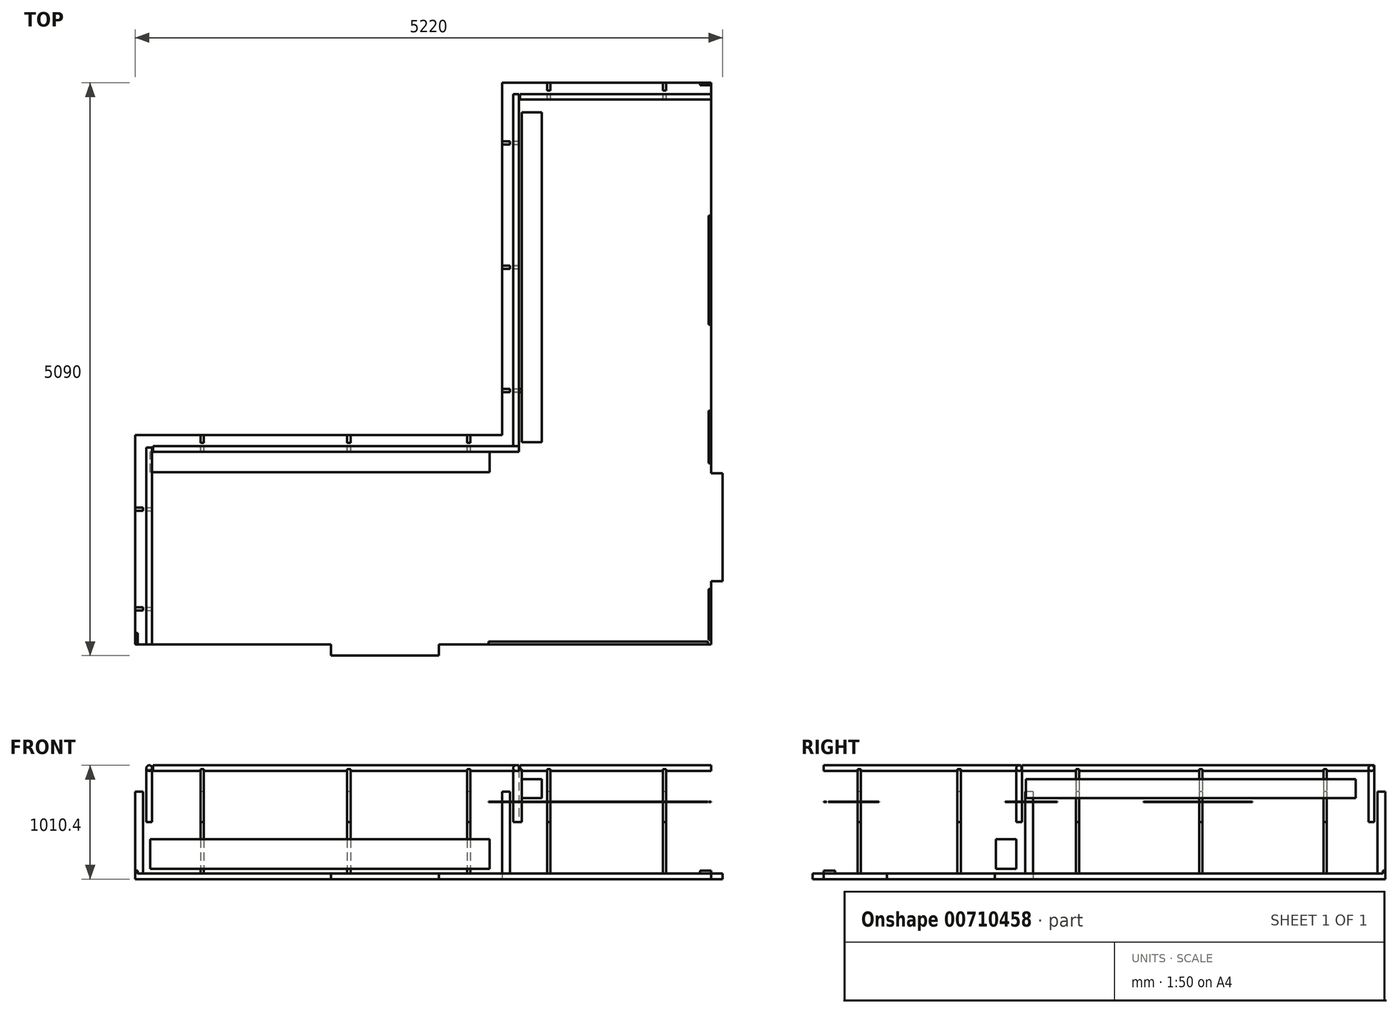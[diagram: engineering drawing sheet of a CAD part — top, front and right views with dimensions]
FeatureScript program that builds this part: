
annotation { "Feature Type Name" : "Feature", "Feature Type Description" : "" }
export const myFeature = defineFeature(function(context is Context, id is Id, definition is map)
    precondition{}
    {
        {
            var Q0;
            Q0=qCreatedBy(makeId("Top.planeOp"),FACE);
            var sketch = newSketch(context, id + "F0", { "sketchPlane" : qUnion([Q0])});
            skLineSegment(sketch, "E0", {"start": v(0, 0) * mm, "end": v(0, 560) * mm});
            skLineSegment(sketch, "E1", {"start": v(0, 4990) * mm, "end": v(-1860, 4990) * mm});
            skLineSegment(sketch, "E2", {"start": v(-1860, 4990) * mm, "end": v(-1860, 1860) * mm});
            skLineSegment(sketch, "E3", {"start": v(-1860, 1860) * mm, "end": v(-5120, 1860) * mm});
            skLineSegment(sketch, "E4", {"start": v(-5120, 1860) * mm, "end": v(-5120, 0) * mm});
            skLineSegment(sketch, "E5", {"start": v(-5120, 0) * mm, "end": v(-3380, 0) * mm});
            skLineSegment(sketch, "E6", {"start": v(0, 1520) * mm, "end": v(100, 1520) * mm});
            skLineSegment(sketch, "E7", {"start": v(100, 1520) * mm, "end": v(100, 560) * mm});
            skLineSegment(sketch, "E8", {"start": v(100, 560) * mm, "end": v(0, 560) * mm});
            skLineSegment(sketch, "E9.trimOffspring", {"start": v(0, 1520) * mm, "end": v(0, 4990) * mm});
            skLineSegment(sketch, "E10.trimOffspring", {"start": v(-2420, 0) * mm, "end": v(0, 0) * mm});
            skLineSegment(sketch, "E11", {"start": v(-3380, 0) * mm, "end": v(-3380, -100) * mm});
            skLineSegment(sketch, "E12", {"start": v(-3380, -100) * mm, "end": v(-2420, -100) * mm});
            skLineSegment(sketch, "E13", {"start": v(-2420, -100) * mm, "end": v(-2420, 0) * mm});
            skSolve(sketch);
        }
        {
            var Q0;
            Q0=makeQuery(id+"F0.imprint","IMPRINT",FACE,{"disambiguationData":[TD([[makeQuery(id+"F0.imprint","IMPRINT",EDGE,{"derivedFrom":sQuery(id+"F0.wireOp",EDGE,"E0")}),1.0]])]});
            extrude(context, id + "F1", {"entities" : qUnion([Q0]), "depth" : 25.4 * mm, "offsetDistance" : 25.4 * mm});
        }
        {
            var Q0;
            Q0=makeQuery(id+"F1.opExtrude","CAP_FACE",FACE,{"disambiguationData":[OSD([sQuery(id+"F0.wireOp",EDGE,"E0"),sQuery(id+"F0.wireOp",EDGE,"E1"),sQuery(id+"F0.wireOp",EDGE,"E2"),sQuery(id+"F0.wireOp",EDGE,"E3"),sQuery(id+"F0.wireOp",EDGE,"E4"),sQuery(id+"F0.wireOp",EDGE,"E5"),sQuery(id+"F0.wireOp",EDGE,"E6"),sQuery(id+"F0.wireOp",EDGE,"E7"),sQuery(id+"F0.wireOp",EDGE,"E8"),sQuery(id+"F0.wireOp",EDGE,"E9.trimOffspring"),sQuery(id+"F0.wireOp",EDGE,"E10.trimOffspring"),sQuery(id+"F0.wireOp",EDGE,"E11"),sQuery(id+"F0.wireOp",EDGE,"E12"),sQuery(id+"F0.wireOp",EDGE,"E13")])],"isStart":false});
            var sketch = newSketch(context, id + "F2", { "sketchPlane" : qUnion([Q0])});
            skLineSegment(sketch, "E14.bottom", {"start": v(-430, 4990) * mm, "end": v(-400, 4990) * mm});
            skLineSegment(sketch, "E14.top", {"start": v(-430, 4920) * mm, "end": v(-400, 4920) * mm});
            skLineSegment(sketch, "E14.left", {"start": v(-430, 4990) * mm, "end": v(-430, 4920) * mm});
            skLineSegment(sketch, "E14.right", {"start": v(-400, 4990) * mm, "end": v(-400, 4920) * mm});
            skLineSegment(sketch, "E15.bottom", {"start": v(-1860, 4470) * mm, "end": v(-1790, 4470) * mm});
            skLineSegment(sketch, "E15.top", {"start": v(-1860, 4440) * mm, "end": v(-1790, 4440) * mm});
            skLineSegment(sketch, "E15.left", {"start": v(-1860, 4470) * mm, "end": v(-1860, 4440) * mm});
            skLineSegment(sketch, "E15.right", {"start": v(-1790, 4470) * mm, "end": v(-1790, 4440) * mm});
            skLineSegment(sketch, "E16.bottom", {"start": v(-1860, 2270) * mm, "end": v(-1790, 2270) * mm});
            skLineSegment(sketch, "E16.top", {"start": v(-1860, 2240) * mm, "end": v(-1790, 2240) * mm});
            skLineSegment(sketch, "E16.left", {"start": v(-1860, 2270) * mm, "end": v(-1860, 2240) * mm});
            skLineSegment(sketch, "E16.right", {"start": v(-1790, 2270) * mm, "end": v(-1790, 2240) * mm});
            skLineSegment(sketch, "E17.bottom", {"start": v(-2171.25, 1860) * mm, "end": v(-2141.25, 1860) * mm});
            skLineSegment(sketch, "E17.top", {"start": v(-2171.25, 1790) * mm, "end": v(-2141.25, 1790) * mm});
            skLineSegment(sketch, "E17.left", {"start": v(-2171.25, 1860) * mm, "end": v(-2171.25, 1790) * mm});
            skLineSegment(sketch, "E17.right", {"start": v(-2141.25, 1860) * mm, "end": v(-2141.25, 1790) * mm});
            skLineSegment(sketch, "E18.bottom", {"start": v(-3235.69, 1860) * mm, "end": v(-3205.69, 1860) * mm});
            skLineSegment(sketch, "E18.top", {"start": v(-3235.69, 1790) * mm, "end": v(-3205.69, 1790) * mm});
            skLineSegment(sketch, "E18.left", {"start": v(-3235.69, 1860) * mm, "end": v(-3235.69, 1790) * mm});
            skLineSegment(sketch, "E18.right", {"start": v(-3205.69, 1860) * mm, "end": v(-3205.69, 1790) * mm});
            skLineSegment(sketch, "E19.bottom", {"start": v(-4538.86, 1860) * mm, "end": v(-4508.86, 1860) * mm});
            skLineSegment(sketch, "E19.top", {"start": v(-4538.86, 1790) * mm, "end": v(-4508.86, 1790) * mm});
            skLineSegment(sketch, "E19.left", {"start": v(-4538.86, 1860) * mm, "end": v(-4538.86, 1790) * mm});
            skLineSegment(sketch, "E19.right", {"start": v(-4508.86, 1860) * mm, "end": v(-4508.86, 1790) * mm});
            skLineSegment(sketch, "E20.bottom", {"start": v(-1460, 4990) * mm, "end": v(-1430, 4990) * mm});
            skLineSegment(sketch, "E20.top", {"start": v(-1460, 4920) * mm, "end": v(-1430, 4920) * mm});
            skLineSegment(sketch, "E20.left", {"start": v(-1460, 4990) * mm, "end": v(-1460, 4920) * mm});
            skLineSegment(sketch, "E20.right", {"start": v(-1430, 4990) * mm, "end": v(-1430, 4920) * mm});
            skLineSegment(sketch, "E21.bottom", {"start": v(-5120, 300) * mm, "end": v(-5050, 300) * mm});
            skLineSegment(sketch, "E21.top", {"start": v(-5120, 330) * mm, "end": v(-5050, 330) * mm});
            skLineSegment(sketch, "E21.left", {"start": v(-5120, 300) * mm, "end": v(-5120, 330) * mm});
            skLineSegment(sketch, "E21.right", {"start": v(-5050, 300) * mm, "end": v(-5050, 330) * mm});
            skLineSegment(sketch, "E22.bottom", {"start": v(-1860, 3335) * mm, "end": v(-1790, 3335) * mm});
            skLineSegment(sketch, "E22.top", {"start": v(-1860, 3365) * mm, "end": v(-1790, 3365) * mm});
            skLineSegment(sketch, "E22.left", {"start": v(-1860, 3335) * mm, "end": v(-1860, 3365) * mm});
            skLineSegment(sketch, "E22.right", {"start": v(-1790, 3335) * mm, "end": v(-1790, 3365) * mm});
            skLineSegment(sketch, "E23.bottom", {"start": v(-5120, 1216.35) * mm, "end": v(-5050, 1216.35) * mm});
            skLineSegment(sketch, "E23.top", {"start": v(-5120, 1186.35) * mm, "end": v(-5050, 1186.35) * mm});
            skLineSegment(sketch, "E23.left", {"start": v(-5120, 1216.35) * mm, "end": v(-5120, 1186.35) * mm});
            skLineSegment(sketch, "E23.right", {"start": v(-5050, 1216.35) * mm, "end": v(-5050, 1186.35) * mm});
            skSolve(sketch);
        }
        {
            var Q0;
            Q0 = qSketchRegion(id + "F2", true);
            extrude(context, id + "F3", {"entities" : qUnion([Q0]), "operationType" : NewBodyOperationType.ADD, "depth" : 750 * mm, "offsetDistance" : 25 * mm});
        }
        {
            var Q0;
            Q0=makeQuery(id+"F1.opExtrude","CAP_FACE",FACE,{"disambiguationData":[OSD([sQuery(id+"F0.wireOp",EDGE,"E0"),sQuery(id+"F0.wireOp",EDGE,"E1"),sQuery(id+"F0.wireOp",EDGE,"E2"),sQuery(id+"F0.wireOp",EDGE,"E3"),sQuery(id+"F0.wireOp",EDGE,"E4"),sQuery(id+"F0.wireOp",EDGE,"E5"),sQuery(id+"F0.wireOp",EDGE,"E6"),sQuery(id+"F0.wireOp",EDGE,"E7"),sQuery(id+"F0.wireOp",EDGE,"E8"),sQuery(id+"F0.wireOp",EDGE,"E9.trimOffspring"),sQuery(id+"F0.wireOp",EDGE,"E10.trimOffspring"),sQuery(id+"F0.wireOp",EDGE,"E11"),sQuery(id+"F0.wireOp",EDGE,"E12"),sQuery(id+"F0.wireOp",EDGE,"E13")])],"isStart":false});
            cPlane(context, id + "F4", {"entities" : qUnion([Q0]), "cplaneType" : CPlaneType.OFFSET, "offset" : 480 * mm, "width" : 150 * mm, "height" : 150 * mm});
        }
        {
            var Q0;
            Q0=qCreatedBy(id+"F4.planeOp",FACE);
            var sketch = newSketch(context, id + "F5", { "sketchPlane" : qUnion([Q0])});
            skPoint(sketch, "E24.oppositeSnap0", {"position": v(-1825, 4470) * mm});
            skLineSegment(sketch, "E24.bottom", {"start": v(-1760, 4440) * mm, "end": v(-1710, 4440) * mm});
            skLineSegment(sketch, "E24.top", {"start": v(-1760, 4470) * mm, "end": v(-1710, 4470) * mm});
            skLineSegment(sketch, "E24.left", {"start": v(-1760, 4440) * mm, "end": v(-1760, 4470) * mm});
            skLineSegment(sketch, "E24.right", {"start": v(-1710, 4440) * mm, "end": v(-1710, 4470) * mm});
            skLineSegment(sketch, "E25.bottom", {"start": v(-1460, 4890) * mm, "end": v(-1430, 4890) * mm});
            skLineSegment(sketch, "E25.top", {"start": v(-1460, 4840) * mm, "end": v(-1430, 4840) * mm});
            skLineSegment(sketch, "E25.left", {"start": v(-1460, 4890) * mm, "end": v(-1460, 4840) * mm});
            skLineSegment(sketch, "E25.right", {"start": v(-1430, 4890) * mm, "end": v(-1430, 4840) * mm});
            skPoint(sketch, "E26.oppositeSnap0", {"position": v(-400, 4955) * mm});
            skLineSegment(sketch, "E26.bottom", {"start": v(-430, 4890) * mm, "end": v(-400, 4890) * mm});
            skLineSegment(sketch, "E26.top", {"start": v(-430, 4840) * mm, "end": v(-400, 4840) * mm});
            skLineSegment(sketch, "E26.left", {"start": v(-430, 4890) * mm, "end": v(-430, 4840) * mm});
            skLineSegment(sketch, "E26.right", {"start": v(-400, 4890) * mm, "end": v(-400, 4840) * mm});
            skLineSegment(sketch, "E27.bottom", {"start": v(-1760, 2270) * mm, "end": v(-1710, 2270) * mm});
            skLineSegment(sketch, "E27.top", {"start": v(-1760, 2240) * mm, "end": v(-1710, 2240) * mm});
            skLineSegment(sketch, "E27.left", {"start": v(-1760, 2270) * mm, "end": v(-1760, 2240) * mm});
            skLineSegment(sketch, "E27.right", {"start": v(-1710, 2270) * mm, "end": v(-1710, 2240) * mm});
            skLineSegment(sketch, "E28.bottom", {"start": v(-2171.25, 1760) * mm, "end": v(-2141.25, 1760) * mm});
            skLineSegment(sketch, "E28.top", {"start": v(-2171.25, 1710) * mm, "end": v(-2141.25, 1710) * mm});
            skLineSegment(sketch, "E28.left", {"start": v(-2171.25, 1760) * mm, "end": v(-2171.25, 1710) * mm});
            skLineSegment(sketch, "E28.right", {"start": v(-2141.25, 1760) * mm, "end": v(-2141.25, 1710) * mm});
            skLineSegment(sketch, "E29.bottom", {"start": v(-3235.69, 1710) * mm, "end": v(-3205.69, 1710) * mm});
            skLineSegment(sketch, "E29.top", {"start": v(-3235.69, 1760) * mm, "end": v(-3205.69, 1760) * mm});
            skLineSegment(sketch, "E29.left", {"start": v(-3235.69, 1710) * mm, "end": v(-3235.69, 1760) * mm});
            skLineSegment(sketch, "E29.right", {"start": v(-3205.69, 1710) * mm, "end": v(-3205.69, 1760) * mm});
            skLineSegment(sketch, "E30.bottom", {"start": v(-4538.86, 1760) * mm, "end": v(-4508.86, 1760) * mm});
            skLineSegment(sketch, "E30.top", {"start": v(-4538.86, 1710) * mm, "end": v(-4508.86, 1710) * mm});
            skLineSegment(sketch, "E30.left", {"start": v(-4538.86, 1760) * mm, "end": v(-4538.86, 1710) * mm});
            skLineSegment(sketch, "E30.right", {"start": v(-4508.86, 1760) * mm, "end": v(-4508.86, 1710) * mm});
            skLineSegment(sketch, "E31.bottom", {"start": v(-5020, 330) * mm, "end": v(-4970, 330) * mm});
            skLineSegment(sketch, "E31.top", {"start": v(-5020, 300) * mm, "end": v(-4970, 300) * mm});
            skLineSegment(sketch, "E31.left", {"start": v(-4970, 330) * mm, "end": v(-4970, 300) * mm});
            skLineSegment(sketch, "E31.right", {"start": v(-5020, 330) * mm, "end": v(-5020, 300) * mm});
            skLineSegment(sketch, "E32.bottom", {"start": v(-5020, 1216.35) * mm, "end": v(-4970, 1216.35) * mm});
            skLineSegment(sketch, "E32.top", {"start": v(-5020, 1186.35) * mm, "end": v(-4970, 1186.35) * mm});
            skLineSegment(sketch, "E32.left", {"start": v(-5020, 1216.35) * mm, "end": v(-5020, 1186.35) * mm});
            skLineSegment(sketch, "E32.right", {"start": v(-4970, 1216.35) * mm, "end": v(-4970, 1186.35) * mm});
            skLineSegment(sketch, "E33.bottom", {"start": v(-1760, 3365) * mm, "end": v(-1710, 3365) * mm});
            skLineSegment(sketch, "E33.top", {"start": v(-1760, 3335) * mm, "end": v(-1710, 3335) * mm});
            skLineSegment(sketch, "E33.left", {"start": v(-1760, 3365) * mm, "end": v(-1760, 3335) * mm});
            skLineSegment(sketch, "E33.right", {"start": v(-1710, 3365) * mm, "end": v(-1710, 3335) * mm});
            skSolve(sketch);
        }
        {
            var Q0;
            Q0 = qSketchRegion(id + "F5", true);
            extrude(context, id + "F6", {"entities" : qUnion([Q0]), "operationType" : NewBodyOperationType.ADD, "depth" : 470 * mm, "offsetDistance" : 25 * mm});
        }
        {
            var Q0;
            Q0=makeQuery(id+"F1.opExtrude","SWEPT_FACE",FACE,{"disambiguationData":[OSD([sQuery(id+"F0.wireOp",EDGE,"E9.trimOffspring")])]});
            var sketch = newSketch(context, id + "F7", { "sketchPlane" : qUnion([Q0])});
            skCircle(sketch, "E34", {"center": v(4865, 985.4) * mm, "radius": 25 * mm});
            skLineSegment(sketch, "E35", {"start": v(4865, 985.4) * mm, "end": v(4865, 975.4) * mm, "construction": true});
            skSolve(sketch);
        }
        {
            var Q0;
            Q0 = qSketchRegion(id + "F7", true);
            var Q1;
            Q1=makeQuery(id+"F3.boolean.opBoolean","MERGE",FACE,{"derivedFrom":[makeQuery(id+"F1.opExtrude","SWEPT_FACE",FACE,{"disambiguationData":[OSD([sQuery(id+"F0.wireOp",EDGE,"E2")])]}),makeQuery(id+"F3.opExtrude","SWEPT_FACE",FACE,{"disambiguationData":[OSD([sQuery(id+"F2.wireOp",EDGE,"E15.left")])]}),makeQuery(id+"F3.opExtrude","SWEPT_FACE",FACE,{"disambiguationData":[OSD([sQuery(id+"F2.wireOp",EDGE,"E16.left")])]})]});
            extrude(context, id + "F8", {"entities" : qUnion([Q0]), "operationType" : NewBodyOperationType.ADD, "oppositeDirection" : true, "depth" : 1700 * mm, "endBoundEntityFace" : qUnion([Q1]), "offsetDistance" : 25 * mm});
        }
        {
            var Q0;
            Q0=makeQuery(id+"F6.opExtrude","SWEPT_FACE",FACE,{"disambiguationData":[OSD([sQuery(id+"F5.wireOp",EDGE,"E25.bottom")])]});
            var sketch = newSketch(context, id + "F9", { "sketchPlane" : qUnion([Q0])});
            skCircle(sketch, "E36", {"center": v(1735, 985.4) * mm, "radius": 25 * mm});
            skLineSegment(sketch, "E37", {"start": v(1735, 985.4) * mm, "end": v(1735, 975.4) * mm, "construction": true});
            skSolve(sketch);
        }
        {
            var Q0;
            Q0=makeQuery(id+"F9.imprint","IMPRINT",FACE,{"disambiguationData":[TD([[makeQuery(id+"F9.imprint","IMPRINT",EDGE,{"derivedFrom":sQuery(id+"F9.wireOp",EDGE,"E36")}),1.0]])]});
            extrude(context, id + "F10", {"entities" : qUnion([Q0]), "operationType" : NewBodyOperationType.ADD, "oppositeDirection" : true, "depth" : 3130 * mm, "offsetDistance" : 25 * mm});
        }
        {
            var Q0;
            Q0=makeQuery(id+"F6.opExtrude","SWEPT_FACE",FACE,{"disambiguationData":[OSD([sQuery(id+"F5.wireOp",EDGE,"E27.right")])]});
            var sketch = newSketch(context, id + "F11", { "sketchPlane" : qUnion([Q0])});
            skCircle(sketch, "E38", {"center": v(1735, 985.4) * mm, "radius": 25 * mm});
            skLineSegment(sketch, "E39", {"start": v(1735, 985.4) * mm, "end": v(1735, 975.4) * mm, "construction": true});
            skSolve(sketch);
        }
        {
            var Q0;
            Q0 = qSketchRegion(id + "F11", true);
            var Q1;
            Q1=makeQuery(id+"F3.boolean.opBoolean","MERGE",FACE,{"derivedFrom":[makeQuery(id+"F1.opExtrude","SWEPT_FACE",FACE,{"disambiguationData":[OSD([sQuery(id+"F0.wireOp",EDGE,"E4")])]}),makeQuery(id+"F3.opExtrude","SWEPT_FACE",FACE,{"disambiguationData":[OSD([sQuery(id+"F2.wireOp",EDGE,"E21.left")])]}),makeQuery(id+"F3.opExtrude","SWEPT_FACE",FACE,{"disambiguationData":[OSD([sQuery(id+"F2.wireOp",EDGE,"E23.left")])]})]});
            extrude(context, id + "F12", {"entities" : qUnion([Q0]), "operationType" : NewBodyOperationType.ADD, "oppositeDirection" : true, "depth" : 3250 * mm, "endBoundEntityFace" : qUnion([Q1]), "offsetDistance" : 25 * mm});
        }
        {
            var Q0;
            Q0=makeQuery(id+"F1.opExtrude","SWEPT_FACE",FACE,{"disambiguationData":[OSD([sQuery(id+"F0.wireOp",EDGE,"E5")])]});
            var sketch = newSketch(context, id + "F13", { "sketchPlane" : qUnion([Q0])});
            skCircle(sketch, "E40", {"center": v(-4995, 985.4) * mm, "radius": 25 * mm});
            skLineSegment(sketch, "E41", {"start": v(-4995, 985.4) * mm, "end": v(-4995, 975.4) * mm, "construction": true});
            skSolve(sketch);
        }
        {
            var Q0;
            Q0 = qSketchRegion(id + "F13", true);
            var Q1;
            Q1=makeQuery(id+"F3.boolean.opBoolean","MERGE",FACE,{"derivedFrom":[makeQuery(id+"F1.opExtrude","SWEPT_FACE",FACE,{"disambiguationData":[OSD([sQuery(id+"F0.wireOp",EDGE,"E3")])]}),makeQuery(id+"F3.opExtrude","SWEPT_FACE",FACE,{"disambiguationData":[OSD([sQuery(id+"F2.wireOp",EDGE,"E17.bottom")])]}),makeQuery(id+"F3.opExtrude","SWEPT_FACE",FACE,{"disambiguationData":[OSD([sQuery(id+"F2.wireOp",EDGE,"E18.bottom")])]}),makeQuery(id+"F3.opExtrude","SWEPT_FACE",FACE,{"disambiguationData":[OSD([sQuery(id+"F2.wireOp",EDGE,"E19.bottom")])]})]});
            extrude(context, id + "F14", {"entities" : qUnion([Q0]), "oppositeDirection" : true, "depth" : 1750 * mm, "endBoundEntityFace" : qUnion([Q1]), "offsetDistance" : 25 * mm});
        }
        {
            var Q0;
            Q0=makeQuery(id+"F1.opExtrude","CAP_FACE",FACE,{"disambiguationData":[OSD([sQuery(id+"F0.wireOp",EDGE,"E0"),sQuery(id+"F0.wireOp",EDGE,"E1"),sQuery(id+"F0.wireOp",EDGE,"E2"),sQuery(id+"F0.wireOp",EDGE,"E3"),sQuery(id+"F0.wireOp",EDGE,"E4"),sQuery(id+"F0.wireOp",EDGE,"E5"),sQuery(id+"F0.wireOp",EDGE,"E6"),sQuery(id+"F0.wireOp",EDGE,"E7"),sQuery(id+"F0.wireOp",EDGE,"E8"),sQuery(id+"F0.wireOp",EDGE,"E9.trimOffspring"),sQuery(id+"F0.wireOp",EDGE,"E10.trimOffspring"),sQuery(id+"F0.wireOp",EDGE,"E11"),sQuery(id+"F0.wireOp",EDGE,"E12"),sQuery(id+"F0.wireOp",EDGE,"E13")])],"isStart":false});
            cPlane(context, id + "F15", {"entities" : qUnion([Q0]), "cplaneType" : CPlaneType.OFFSET, "offset" : 660 * mm, "width" : 150 * mm, "height" : 150 * mm});
        }
        {
            var Q0;
            Q0=qCreatedBy(id+"F15.planeOp",FACE);
            var sketch = newSketch(context, id + "F16", { "sketchPlane" : qUnion([Q0])});
            skLineSegment(sketch, "E42.bottom", {"start": v(0, 3810) * mm, "end": v(-25, 3810) * mm});
            skLineSegment(sketch, "E42.top", {"start": v(0, 2840) * mm, "end": v(-25, 2840) * mm});
            skLineSegment(sketch, "E42.left", {"start": v(0, 3810) * mm, "end": v(0, 2840) * mm});
            skLineSegment(sketch, "E42.right", {"start": v(-25, 3810) * mm, "end": v(-25, 2840) * mm});
            skLineSegment(sketch, "E43.bottom", {"start": v(0, 2075) * mm, "end": v(-25, 2075) * mm});
            skLineSegment(sketch, "E43.top", {"start": v(0, 1610) * mm, "end": v(-25, 1610) * mm});
            skLineSegment(sketch, "E43.left", {"start": v(0, 2075) * mm, "end": v(0, 1610) * mm});
            skLineSegment(sketch, "E43.right", {"start": v(-25, 2075) * mm, "end": v(-25, 1610) * mm});
            skLineSegment(sketch, "E44.bottom", {"start": v(-30, 0) * mm, "end": v(-1980, 0) * mm});
            skLineSegment(sketch, "E44.top", {"start": v(-30, 25) * mm, "end": v(-1980, 25) * mm});
            skLineSegment(sketch, "E44.left", {"start": v(-30, 0) * mm, "end": v(-30, 25) * mm});
            skLineSegment(sketch, "E44.right", {"start": v(-1980, 0) * mm, "end": v(-1980, 25) * mm});
            skLineSegment(sketch, "E45.bottom", {"start": v(0, 490) * mm, "end": v(-25, 490) * mm});
            skLineSegment(sketch, "E45.top", {"start": v(0, 40) * mm, "end": v(-25, 40) * mm});
            skLineSegment(sketch, "E45.left", {"start": v(0, 490) * mm, "end": v(0, 40) * mm});
            skLineSegment(sketch, "E45.right", {"start": v(-25, 490) * mm, "end": v(-25, 40) * mm});
            skSolve(sketch);
        }
        {
            var Q0;
            Q0 = qSketchRegion(id + "F16", true);
            extrude(context, id + "F17", {"entities" : qUnion([Q0]), "operationType" : NewBodyOperationType.ADD, "depth" : 3 * mm, "offsetDistance" : 25 * mm});
        }
        {
            var Q0;
            Q0=makeQuery(id+"F2.imprint","IMPRINT",FACE,{"disambiguationData":[TD([[makeQuery(id+"F2.imprint","IMPRINT",EDGE,{"derivedFrom":sQuery(id+"F2.wireOp",EDGE,"E14.top")}),-1.0]])]});
            extrude(context, id + "F18", {"entities" : qUnion([Q0]), "operationType" : NewBodyOperationType.ADD, "depth" : 25 * mm, "offsetDistance" : 25 * mm});
        }
        {
            var Q0;
            Q0=makeQuery(id+"F18.opExtrude","CAP_FACE",FACE,{"disambiguationData":[OSD([sQuery(id+"F0.wireOp",EDGE,"E0"),sQuery(id+"F0.wireOp",EDGE,"E1"),sQuery(id+"F0.wireOp",EDGE,"E2"),sQuery(id+"F0.wireOp",EDGE,"E3"),sQuery(id+"F0.wireOp",EDGE,"E4"),sQuery(id+"F0.wireOp",EDGE,"E5"),sQuery(id+"F0.wireOp",EDGE,"E6"),sQuery(id+"F0.wireOp",EDGE,"E7"),sQuery(id+"F0.wireOp",EDGE,"E8"),sQuery(id+"F0.wireOp",EDGE,"E9.trimOffspring"),sQuery(id+"F0.wireOp",EDGE,"E10.trimOffspring"),sQuery(id+"F0.wireOp",EDGE,"E11"),sQuery(id+"F0.wireOp",EDGE,"E12"),sQuery(id+"F0.wireOp",EDGE,"E13"),sQuery(id+"F2.wireOp",EDGE,"E14.top"),sQuery(id+"F2.wireOp",EDGE,"E14.left"),sQuery(id+"F2.wireOp",EDGE,"E14.right"),sQuery(id+"F2.wireOp",EDGE,"E15.bottom"),sQuery(id+"F2.wireOp",EDGE,"E15.top"),sQuery(id+"F2.wireOp",EDGE,"E15.right"),sQuery(id+"F2.wireOp",EDGE,"E16.bottom"),sQuery(id+"F2.wireOp",EDGE,"E16.top"),sQuery(id+"F2.wireOp",EDGE,"E16.right"),sQuery(id+"F2.wireOp",EDGE,"E17.top"),sQuery(id+"F2.wireOp",EDGE,"E17.left"),sQuery(id+"F2.wireOp",EDGE,"E17.right"),sQuery(id+"F2.wireOp",EDGE,"E18.top"),sQuery(id+"F2.wireOp",EDGE,"E18.left"),sQuery(id+"F2.wireOp",EDGE,"E18.right"),sQuery(id+"F2.wireOp",EDGE,"E19.top"),sQuery(id+"F2.wireOp",EDGE,"E19.left"),sQuery(id+"F2.wireOp",EDGE,"E19.right"),sQuery(id+"F2.wireOp",EDGE,"E20.top"),sQuery(id+"F2.wireOp",EDGE,"E20.left"),sQuery(id+"F2.wireOp",EDGE,"E20.right"),sQuery(id+"F2.wireOp",EDGE,"E21.bottom"),sQuery(id+"F2.wireOp",EDGE,"E21.top"),sQuery(id+"F2.wireOp",EDGE,"E21.right"),sQuery(id+"F2.wireOp",EDGE,"E22.bottom"),sQuery(id+"F2.wireOp",EDGE,"E22.top"),sQuery(id+"F2.wireOp",EDGE,"E22.right"),sQuery(id+"F2.wireOp",EDGE,"E23.bottom"),sQuery(id+"F2.wireOp",EDGE,"E23.top"),sQuery(id+"F2.wireOp",EDGE,"E23.right")])],"isStart":false});
            var sketch = newSketch(context, id + "F19", { "sketchPlane" : qUnion([Q0])});
            skLineSegment(sketch, "E46.bottom", {"start": v(0, 4990) * mm, "end": v(-100, 4990) * mm});
            skLineSegment(sketch, "E46.top", {"start": v(0, 4968) * mm, "end": v(-100, 4968) * mm});
            skLineSegment(sketch, "E46.left", {"start": v(0, 4990) * mm, "end": v(0, 4968) * mm});
            skLineSegment(sketch, "E46.right", {"start": v(-100, 4990) * mm, "end": v(-100, 4968) * mm});
            skLineSegment(sketch, "E47.bottom", {"start": v(-5120, 0) * mm, "end": v(-5098, 0) * mm});
            skLineSegment(sketch, "E47.top", {"start": v(-5120, 100) * mm, "end": v(-5098, 100) * mm});
            skLineSegment(sketch, "E47.left", {"start": v(-5120, 0) * mm, "end": v(-5120, 100) * mm});
            skLineSegment(sketch, "E47.right", {"start": v(-5098, 0) * mm, "end": v(-5098, 100) * mm});
            skSolve(sketch);
        }
        {
            var Q0;
            Q0 = qSketchRegion(id + "F19", true);
            extrude(context, id + "F20", {"entities" : qUnion([Q0]), "operationType" : NewBodyOperationType.ADD, "depth" : 25 * mm, "offsetDistance" : 25 * mm});
        }
        {
            var Q0;
            Q0=makeQuery(id+"F6.opExtrude","SWEPT_FACE",FACE,{"disambiguationData":[OSD([sQuery(id+"F5.wireOp",EDGE,"E27.right")])]});
            extrude(context, id + "F21", {"entities" : qUnion([Q0]), "operationType" : NewBodyOperationType.ADD, "depth" : 25 * mm, "offsetDistance" : 25 * mm});
        }
        {
            var Q0;
            Q0=makeQuery(id+"F21.opExtrude","CAP_FACE",FACE,{"disambiguationData":[OSD([sQuery(id+"F5.wireOp",EDGE,"E27.right")])],"isStart":false});
            var sketch = newSketch(context, id + "F22", { "sketchPlane" : qUnion([Q0])});
            skLineSegment(sketch, "E48.bottom", {"start": v(1795.68, 720.4) * mm, "end": v(4727.54, 720.4) * mm});
            skLineSegment(sketch, "E48.top", {"start": v(1795.68, 888.98) * mm, "end": v(4727.54, 888.98) * mm});
            skLineSegment(sketch, "E48.left", {"start": v(1795.68, 720.4) * mm, "end": v(1795.68, 888.98) * mm});
            skLineSegment(sketch, "E48.right", {"start": v(4727.54, 720.4) * mm, "end": v(4727.54, 888.98) * mm});
            skSolve(sketch);
        }
        {
            var Q0;
            Q0 = qSketchRegion(id + "F22", true);
            extrude(context, id + "F23", {"entities" : qUnion([Q0]), "operationType" : NewBodyOperationType.ADD, "depth" : 180 * mm, "offsetDistance" : 25 * mm});
        }
        {
            var Q0;
            Q0=makeQuery(id+"F6.opExtrude","SWEPT_FACE",FACE,{"disambiguationData":[OSD([sQuery(id+"F5.wireOp",EDGE,"E28.top")])]});
            var sketch = newSketch(context, id + "F24", { "sketchPlane" : qUnion([Q0])});
            skLineSegment(sketch, "E49.bottom", {"start": v(-1970.1, 91.5) * mm, "end": v(-4986.84, 91.5) * mm});
            skLineSegment(sketch, "E49.top", {"start": v(-1970.1, 353.31) * mm, "end": v(-4986.84, 353.31) * mm});
            skLineSegment(sketch, "E49.left", {"start": v(-1970.1, 91.5) * mm, "end": v(-1970.1, 353.31) * mm});
            skLineSegment(sketch, "E49.right", {"start": v(-4986.84, 91.5) * mm, "end": v(-4986.84, 353.31) * mm});
            skSolve(sketch);
        }
        {
            var Q0;
            Q0 = qSketchRegion(id + "F24", true);
            extrude(context, id + "F25", {"entities" : qUnion([Q0]), "depth" : 180 * mm, "offsetDistance" : 25 * mm});
        }
    });
